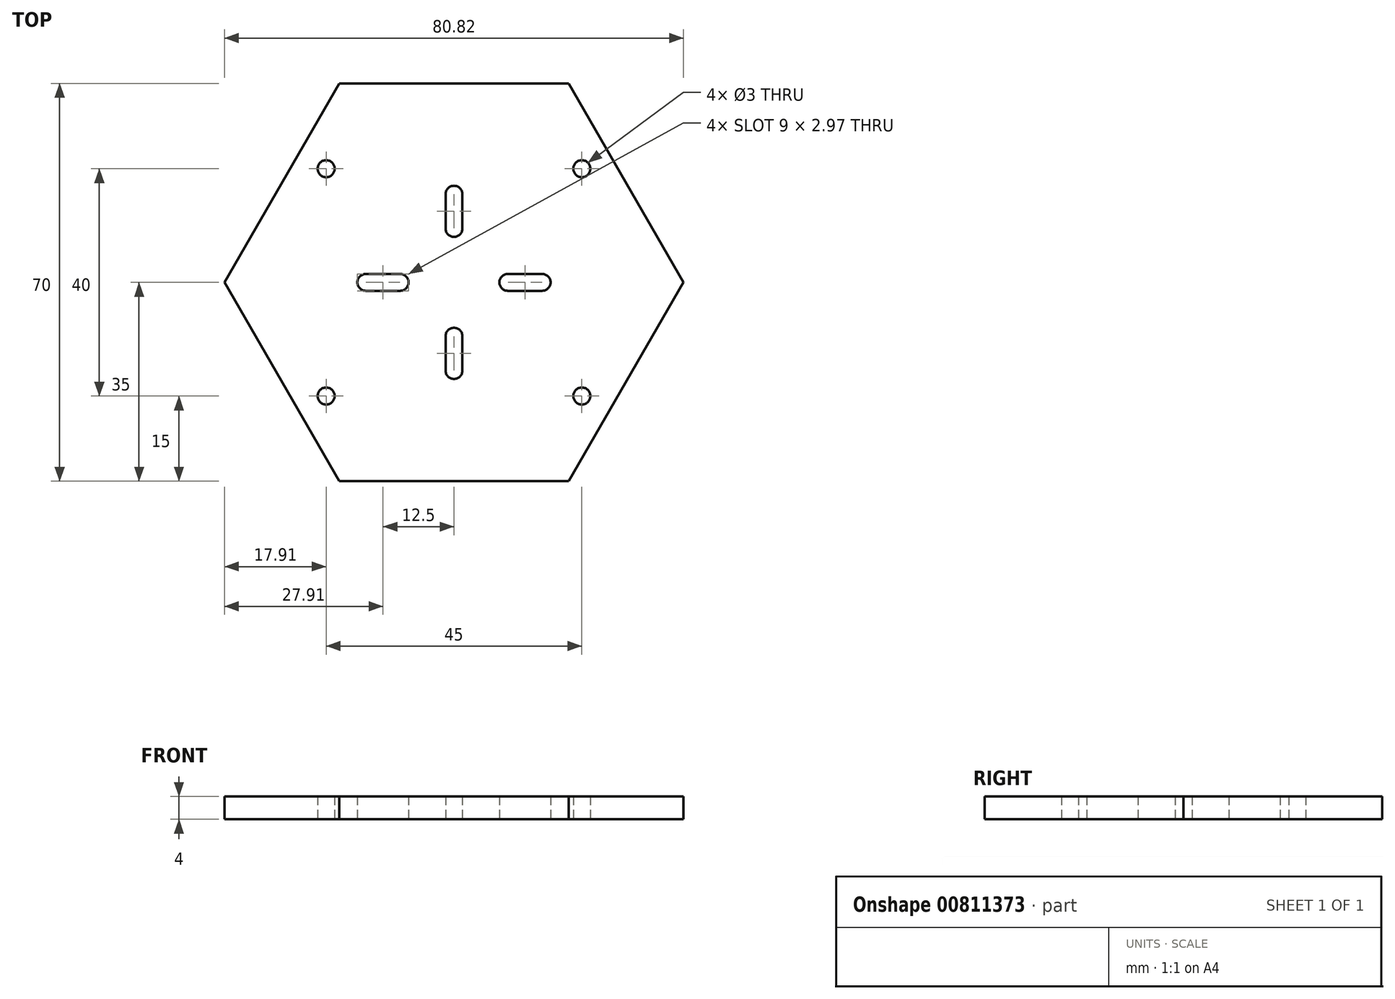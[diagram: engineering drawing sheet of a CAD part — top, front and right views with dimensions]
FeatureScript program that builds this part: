
annotation { "Feature Type Name" : "Feature", "Feature Type Description" : "" }
export const myFeature = defineFeature(function(context is Context, id is Id, definition is map)
    precondition{}
    {
        {
            var Q0;
            Q0=qCreatedBy(makeId("Top.planeOp"),FACE);
            var sketch = newSketch(context, id + "F0", { "sketchPlane" : qUnion([Q0])});
            skLineSegment(sketch, "E0.bottom", {"start": v(9.49, -1.49) * mm, "end": v(-9.49, -1.49) * mm});
            skLineSegment(sketch, "E0.top", {"start": v(9.49, 1.49) * mm, "end": v(-9.49, 1.49) * mm});
            skLineSegment(sketch, "E0.left", {"start": v(9.49, -1.49) * mm, "end": v(9.49, 1.49) * mm});
            skLineSegment(sketch, "E0.right", {"start": v(-9.49, -1.49) * mm, "end": v(-9.49, 1.49) * mm});
            skPoint(sketch, "E0.middle", {"position": v(0, 0) * mm});
            skLineSegment(sketch, "E1.bottom", {"start": v(1.49, -9.49) * mm, "end": v(-1.49, -9.49) * mm});
            skLineSegment(sketch, "E1.top", {"start": v(1.49, 9.49) * mm, "end": v(-1.49, 9.49) * mm});
            skLineSegment(sketch, "E1.left", {"start": v(1.49, -9.49) * mm, "end": v(1.49, 9.49) * mm});
            skLineSegment(sketch, "E1.right", {"start": v(-1.49, -9.49) * mm, "end": v(-1.49, 9.49) * mm});
            skLineSegment(sketch, "E2.bottom", {"start": v(-1.49, 9.49) * mm, "end": v(1.49, 9.49) * mm});
            skLineSegment(sketch, "E2.top", {"start": v(-1.49, 15.51) * mm, "end": v(1.49, 15.51) * mm});
            skLineSegment(sketch, "E2.left", {"start": v(-1.49, 9.49) * mm, "end": v(-1.49, 15.51) * mm});
            skLineSegment(sketch, "E2.right", {"start": v(1.49, 9.49) * mm, "end": v(1.49, 15.51) * mm});
            skLineSegment(sketch, "E3.1.0", {"start": v(-15.51, -1.49) * mm, "end": v(-15.51, 1.49) * mm});
            skLineSegment(sketch, "E3.1.1", {"start": v(-9.49, 1.49) * mm, "end": v(-15.51, 1.49) * mm});
            skLineSegment(sketch, "E3.1.2", {"start": v(-9.49, 1.49) * mm, "end": v(-9.49, -1.49) * mm});
            skLineSegment(sketch, "E3.1.3", {"start": v(-9.49, -1.49) * mm, "end": v(-15.51, -1.49) * mm});
            skLineSegment(sketch, "E3.2.0", {"start": v(1.49, -15.51) * mm, "end": v(-1.49, -15.51) * mm});
            skLineSegment(sketch, "E3.2.1", {"start": v(-1.49, -9.49) * mm, "end": v(-1.49, -15.51) * mm});
            skLineSegment(sketch, "E3.2.2", {"start": v(-1.49, -9.49) * mm, "end": v(1.49, -9.49) * mm});
            skLineSegment(sketch, "E3.2.3", {"start": v(1.49, -9.49) * mm, "end": v(1.49, -15.51) * mm});
            skLineSegment(sketch, "E3.3.0", {"start": v(15.51, 1.49) * mm, "end": v(15.51, -1.49) * mm});
            skLineSegment(sketch, "E3.3.1", {"start": v(9.49, -1.49) * mm, "end": v(15.51, -1.49) * mm});
            skLineSegment(sketch, "E3.3.3", {"start": v(9.49, 1.49) * mm, "end": v(15.51, 1.49) * mm});
            skCircle(sketch, "E4", {"center": v(-9.49, 0) * mm, "radius": 1.49 * mm});
            skCircle(sketch, "E5", {"center": v(-15.51, 0) * mm, "radius": 1.49 * mm});
            skCircle(sketch, "E6", {"center": v(9.49, 0) * mm, "radius": 1.49 * mm});
            skCircle(sketch, "E7", {"center": v(15.51, 0) * mm, "radius": 1.49 * mm});
            skCircle(sketch, "E8", {"center": v(0, -9.49) * mm, "radius": 1.49 * mm});
            skCircle(sketch, "E9", {"center": v(0, -15.51) * mm, "radius": 1.49 * mm});
            skCircle(sketch, "E10", {"center": v(0, 15.51) * mm, "radius": 1.49 * mm});
            skCircle(sketch, "E11", {"center": v(0, 9.49) * mm, "radius": 1.49 * mm});
            skCircle(sketch, "E12.cCircle", {"center": v(0, 0) * mm, "radius": 35 * mm, "construction": true});
            skLineSegment(sketch, "E12.0", {"start": v(20.2, -35) * mm, "end": v(-20.2, -35) * mm});
            skLineSegment(sketch, "E12.1", {"start": v(-20.2, -35) * mm, "end": v(-40.41, 0) * mm});
            skLineSegment(sketch, "E12.2", {"start": v(-40.41, 0) * mm, "end": v(-20.2, 35) * mm});
            skLineSegment(sketch, "E12.3", {"start": v(-20.2, 35) * mm, "end": v(20.2, 35) * mm});
            skLineSegment(sketch, "E12.4", {"start": v(20.2, 35) * mm, "end": v(40.41, 0) * mm});
            skLineSegment(sketch, "E12.5", {"start": v(40.41, 0) * mm, "end": v(20.2, -35) * mm});
            skPoint(sketch, "E12.0.midPoint", {"position": v(0, -35) * mm});
            skLineSegment(sketch, "E13.bottom", {"start": v(22.5, -20) * mm, "end": v(-22.5, -20) * mm});
            skLineSegment(sketch, "E13.top", {"start": v(22.5, 20) * mm, "end": v(-22.5, 20) * mm});
            skLineSegment(sketch, "E13.left", {"start": v(22.5, -20) * mm, "end": v(22.5, 20) * mm});
            skLineSegment(sketch, "E13.right", {"start": v(-22.5, -20) * mm, "end": v(-22.5, 20) * mm});
            skCircle(sketch, "E14", {"center": v(-22.5, 20) * mm, "radius": 1.5 * mm});
            skCircle(sketch, "E15", {"center": v(22.5, 20) * mm, "radius": 1.5 * mm});
            skCircle(sketch, "E16", {"center": v(22.5, -20) * mm, "radius": 1.5 * mm});
            skCircle(sketch, "E17", {"center": v(-22.5, -20) * mm, "radius": 1.5 * mm});
            skSolve(sketch);
        }
        {
            var Q0;
            Q0=makeQuery(id+"F0.imprint","IMPRINT",FACE,{"disambiguationData":[TD([[makeQuery(id+"F0.imprint","IMPRINT",EDGE,{"derivedFrom":sQuery(id+"F0.wireOp",EDGE,"E12.0")}),-1.0]])]});
            var Q1;
            {var subQ22=sQuery(id+"F0.wireOp",EDGE,"E2.left");Q1=makeQuery(id+"F0.imprint","IMPRINT",FACE,{"disambiguationData":[TD([[makeQuery(id+"F0.imprint","IMPRINT",EDGE,{"derivedFrom":subQ22}),1.0]])]});}
            var Q2;
            {var subQ0=sQuery(id+"F0.wireOp",EDGE,"E1.left");var subQ1=sQuery(id+"F0.wireOp",EDGE,"E0.top");var subQ2=makeQuery(id+"F0.imprint","INTERSECT",VERTEX,{"derivedFrom":[subQ1,subQ0]});Q2=makeQuery(id+"F0.imprint","IMPRINT",FACE,{"disambiguationData":[TD([[makeQuery(id+"F0.imprint","IMPRINT",EDGE,{"disambiguationData":[TD([[subQ2,-1.0]])],"derivedFrom":subQ1}),-1.0]])]});}
            var Q3;
            {var subQ2=sQuery(id+"F0.wireOp",EDGE,"E0.bottom");var subQ4=sQuery(id+"F0.wireOp",EDGE,"E1.right");var subQ5=makeQuery(id+"F0.imprint","INTERSECT",VERTEX,{"derivedFrom":[subQ2,subQ4]});Q3=makeQuery(id+"F0.imprint","IMPRINT",FACE,{"disambiguationData":[TD([[makeQuery(id+"F0.imprint","IMPRINT",EDGE,{"disambiguationData":[TD([[subQ5,-1.0]])],"derivedFrom":subQ4}),1.0]])]});}
            var Q4;
            {var subQ2=sQuery(id+"F0.wireOp",EDGE,"E0.bottom");var subQ4=sQuery(id+"F0.wireOp",EDGE,"E1.left");var subQ5=makeQuery(id+"F0.imprint","INTERSECT",VERTEX,{"derivedFrom":[subQ2,subQ4]});Q4=makeQuery(id+"F0.imprint","IMPRINT",FACE,{"disambiguationData":[TD([[makeQuery(id+"F0.imprint","IMPRINT",EDGE,{"disambiguationData":[TD([[subQ5,-1.0]])],"derivedFrom":subQ4}),-1.0]])]});}
            var Q5;
            {var subQ0=sQuery(id+"F0.wireOp",EDGE,"E1.left");var subQ1=sQuery(id+"F0.wireOp",EDGE,"E0.bottom");var subQ2=makeQuery(id+"F0.imprint","INTERSECT",VERTEX,{"derivedFrom":[subQ1,subQ0]});Q5=makeQuery(id+"F0.imprint","IMPRINT",FACE,{"disambiguationData":[TD([[makeQuery(id+"F0.imprint","IMPRINT",EDGE,{"disambiguationData":[TD([[subQ2,-1.0]])],"derivedFrom":subQ1}),-1.0]])]});}
            var Q6;
            {var subQ0=sQuery(id+"F0.wireOp",EDGE,"E1.left");var subQ1=sQuery(id+"F0.wireOp",EDGE,"E0.bottom");var subQ2=makeQuery(id+"F0.imprint","INTERSECT",VERTEX,{"derivedFrom":[subQ1,subQ0]});Q6=makeQuery(id+"F0.imprint","IMPRINT",FACE,{"disambiguationData":[TD([[makeQuery(id+"F0.imprint","IMPRINT",EDGE,{"disambiguationData":[TD([[subQ2,-1.0]])],"derivedFrom":subQ1}),1.0]])]});}
            extrude(context, id + "F1", {"entities" : qUnion([Q0, Q1, Q2, Q3, Q4, Q5, Q6]), "depth" : 4 * mm, "offsetDistance" : 25 * mm});
        }
    });
